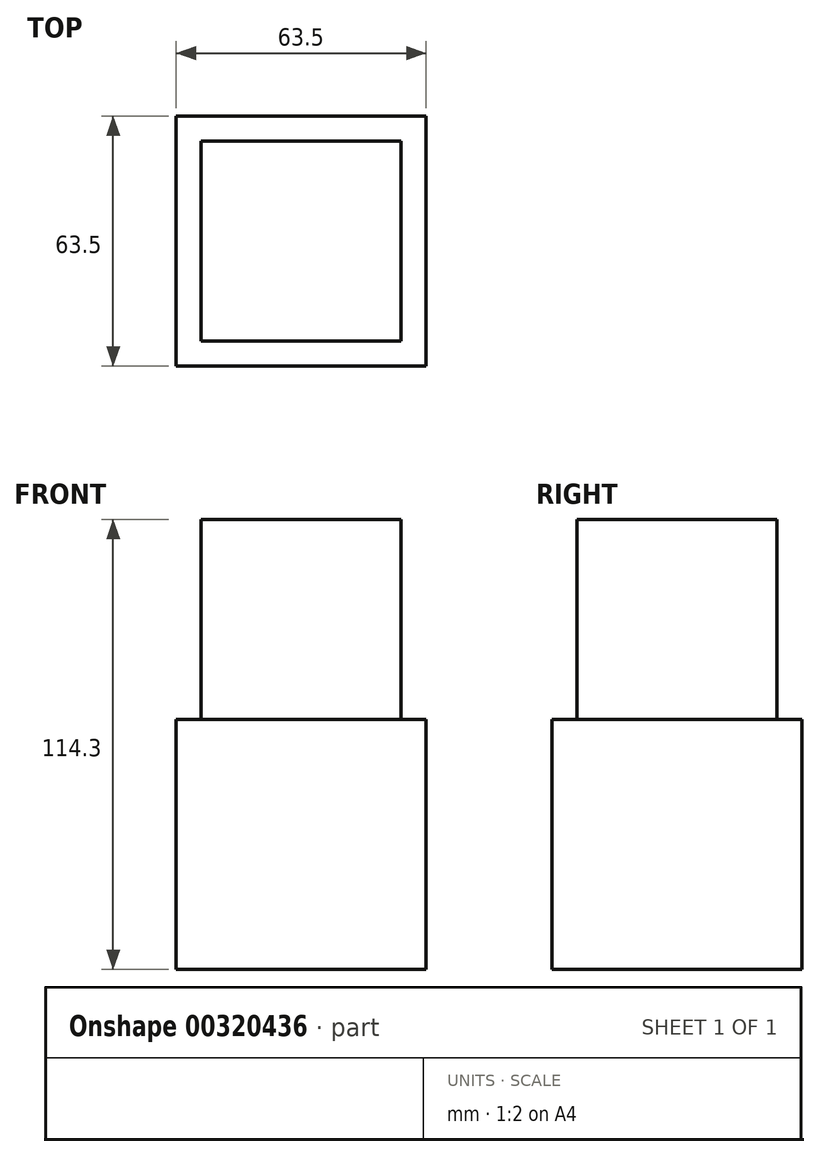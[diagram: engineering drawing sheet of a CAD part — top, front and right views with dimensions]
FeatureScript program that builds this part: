
annotation { "Feature Type Name" : "Feature", "Feature Type Description" : "" }
export const myFeature = defineFeature(function(context is Context, id is Id, definition is map)
    precondition{}
    {
        {
            var Q0;
            Q0=qCreatedBy(makeId("Front.planeOp"),FACE);
            var sketch = newSketch(context, id + "F0", { "sketchPlane" : qUnion([Q0])});
            skLineSegment(sketch, "E0.bottom", {"start": v(31.75, 31.75) * mm, "end": v(-31.75, 31.75) * mm});
            skLineSegment(sketch, "E0.top", {"start": v(31.75, -31.75) * mm, "end": v(-31.75, -31.75) * mm});
            skLineSegment(sketch, "E0.left", {"start": v(31.75, 31.75) * mm, "end": v(31.75, -31.75) * mm});
            skLineSegment(sketch, "E0.right", {"start": v(-31.75, 31.75) * mm, "end": v(-31.75, -31.75) * mm});
            skPoint(sketch, "E0.middle", {"position": v(0, 0) * mm});
            skSolve(sketch);
        }
        {
            var Q0;
            Q0 = qSketchRegion(id + "F0", true);
            extrude(context, id + "F1", {"entities" : qUnion([Q0]), "depth" : 63.5 * mm});
        }
        {
            var Q0;
            Q0=makeQuery(id+"F1.opExtrude","SWEPT_FACE",FACE,{"disambiguationData":[OSD([sQuery(id+"F0.wireOp",EDGE,"E0.bottom")])]});
            var sketch = newSketch(context, id + "F2", { "sketchPlane" : qUnion([Q0])});
            skLineSegment(sketch, "E1.bottom", {"start": v(25.4, -6.35) * mm, "end": v(-25.4, -6.35) * mm});
            skLineSegment(sketch, "E1.top", {"start": v(25.4, -57.15) * mm, "end": v(-25.4, -57.15) * mm});
            skLineSegment(sketch, "E1.left", {"start": v(25.4, -6.35) * mm, "end": v(25.4, -57.15) * mm});
            skLineSegment(sketch, "E1.right", {"start": v(-25.4, -6.35) * mm, "end": v(-25.4, -57.15) * mm});
            skPoint(sketch, "E1.middle", {"position": v(0, -31.75) * mm});
            skPoint(sketch, "E1.middle.positionSnap0", {"position": v(-31.75, -31.75) * mm});
            skPoint(sketch, "E1.middle.positionSnap1", {"position": v(0, -63.5) * mm});
            skPoint(sketch, "E1.centerSnap0", {"position": v(-31.75, -31.75) * mm});
            skPoint(sketch, "E1.centerSnap1", {"position": v(0, -63.5) * mm});
            skSolve(sketch);
        }
        {
            var Q0;
            Q0=makeQuery(id+"F2.imprint","IMPRINT",FACE,{"disambiguationData":[TD([[makeQuery(id+"F2.imprint","IMPRINT",EDGE,{"derivedFrom":sQuery(id+"F2.wireOp",EDGE,"E1.bottom")}),1.0]])]});
            extrude(context, id + "F3", {"entities" : qUnion([Q0]), "operationType" : NewBodyOperationType.ADD, "depth" : 50.8 * mm});
        }
    });
